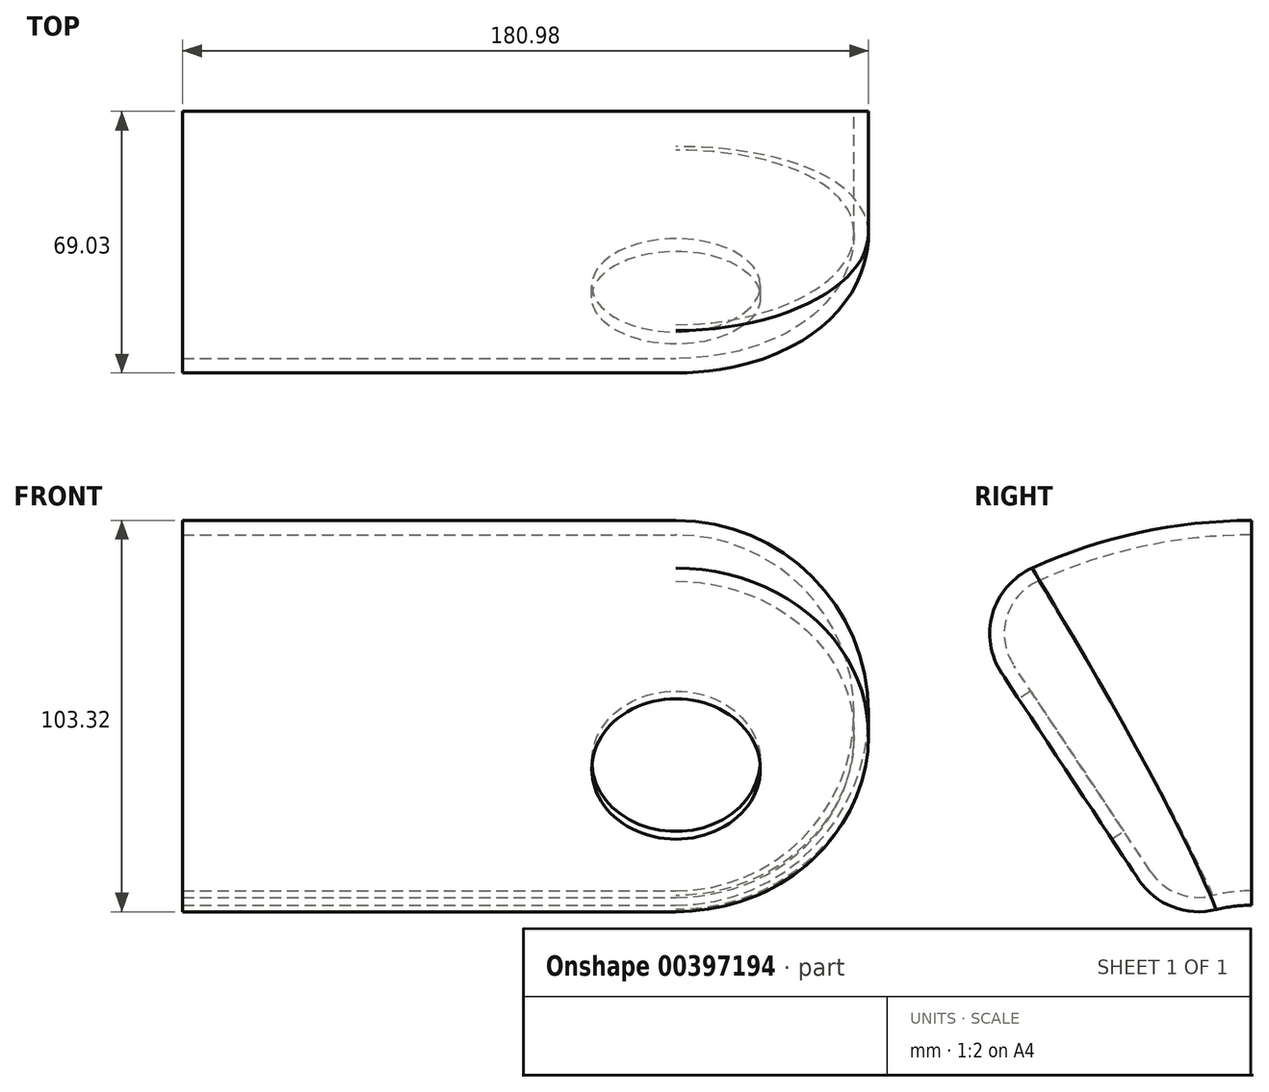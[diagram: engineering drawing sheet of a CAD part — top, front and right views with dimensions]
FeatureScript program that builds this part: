
annotation { "Feature Type Name" : "Feature", "Feature Type Description" : "" }
export const myFeature = defineFeature(function(context is Context, id is Id, definition is map)
    precondition{}
    {
        {
            var Q0;
            Q0=qCreatedBy(makeId("Front.planeOp"),FACE);
            var sketch = newSketch(context, id + "F0", { "sketchPlane" : qUnion([Q0])});
            skLineSegment(sketch, "E0.bottom", {"start": v(0, 0) * mm, "end": v(130.18, 0) * mm});
            skLineSegment(sketch, "E0.top", {"start": v(0, 101.6) * mm, "end": v(130.18, 101.6) * mm});
            skLineSegment(sketch, "E0.left", {"start": v(0, 0) * mm, "end": v(0, 101.6) * mm});
            skLineSegment(sketch, "E0.right", {"start": v(180.98, 0) * mm, "end": v(180.98, 101.6) * mm, "construction": true});
            skLineSegment(sketch, "E1", {"start": v(130.18, 101.6) * mm, "end": v(130.18, 0) * mm, "construction": true});
            skArc(sketch, "E2", {"start": v(130.18, 101.6) * mm, "mid": v(79.38, 50.8) * mm, "end": v(130.18, 0) * mm, "construction": true});
            skArc(sketch, "E3", {"start": v(130.18, 0) * mm, "mid": v(180.98, 50.8) * mm, "end": v(130.18, 101.6) * mm});
            skLineSegment(sketch, "E4", {"start": v(130.18, 101.6) * mm, "end": v(180.98, 101.6) * mm, "construction": true});
            skLineSegment(sketch, "E5", {"start": v(130.18, 0) * mm, "end": v(130.18, 0) * mm});
            skLineSegment(sketch, "E6", {"start": v(130.18, 0) * mm, "end": v(180.98, 0) * mm, "construction": true});
            skCircle(sketch, "E7", {"center": v(130.18, 50.8) * mm, "radius": 22.23 * mm});
            skSolve(sketch);
        }
        {
            var Q0;
            Q0=qCreatedBy(makeId("Right.planeOp"),FACE);
            var sketch = newSketch(context, id + "F1", { "sketchPlane" : qUnion([Q0])});
            skLineSegment(sketch, "E8", {"start": v(0, 0) * mm, "end": v(-25.4, 0) * mm});
            skArc(sketch, "E9", {"start": v(-25.4, 0) * mm, "mid": v(-36.4, -1.62) * mm, "end": v(-46.46, -6.35) * mm});
            skLineSegment(sketch, "E10", {"start": v(-25.4, 0) * mm, "end": v(-25.4, -38.1) * mm});
            skSolve(sketch);
        }
        {
            var Q0;
            Q0=makeQuery(id+"F0.imprint","IMPRINT",FACE,{"disambiguationData":[TD([[makeQuery(id+"F0.imprint","IMPRINT",EDGE,{"derivedFrom":sQuery(id+"F0.wireOp",EDGE,"E0.bottom")}),1.0]])]});
            var Q1;
            Q1=sQuery(id+"F1.wireOp",EDGE,"E8");
            var Q2;
            Q2=sQuery(id+"F1.wireOp",EDGE,"E9");
            sweep(context, id + "F2", {"profiles" : qUnion([Q0]), "path" : qUnion([Q1, Q2])});
        }
        {
            var Q0;
            Q0=makeQuery(id+"F2.opSweep","CAP_EDGE",EDGE,{"disambiguationData":[OSD([sQuery(id+"F0.wireOp",EDGE,"E0.top"),sQuery(id+"F1.wireOp",VERTEX,"E9.end")])],"isStart":false});
            fillet(context, id + "F3", {"entities" : qUnion([Q0]), "radius" : 19.05 * mm, "tangentPropagation" : true, "allowEdgeOverflow" : false});
        }
        {
            var Q0;
            Q0=makeQuery(id+"F2.opSweep","SWEPT_FACE",FACE,{"disambiguationData":[OSD([sQuery(id+"F0.wireOp",EDGE,"E0.left"),sQuery(id+"F1.wireOp",EDGE,"E8")])]});
            var Q1;
            Q1=makeQuery(id+"F2.opSweep","CAP_FACE",FACE,{"disambiguationData":[OSD([sQuery(id+"F0.wireOp",EDGE,"E0.bottom"),sQuery(id+"F0.wireOp",EDGE,"E0.top"),sQuery(id+"F0.wireOp",EDGE,"E0.left"),sQuery(id+"F0.wireOp",EDGE,"E3"),sQuery(id+"F0.wireOp",EDGE,"E7"),sQuery(id+"F1.wireOp",VERTEX,"E8.start")])],"isStart":true});
            var Q2;
            Q2=makeQuery(id+"F2.opSweep","SWEPT_FACE",FACE,{"disambiguationData":[OSD([sQuery(id+"F0.wireOp",EDGE,"E7"),sQuery(id+"F1.wireOp",EDGE,"E9")])]});
            var Q3;
            Q3=makeQuery(id+"F2.opSweep","SWEPT_FACE",FACE,{"disambiguationData":[OSD([sQuery(id+"F0.wireOp",EDGE,"E7"),sQuery(id+"F1.wireOp",EDGE,"E8")])]});
            shell(context, id + "F4", {"entities" : qUnion([Q0, Q1, Q2, Q3]), "thickness" : 3.8 * mm});
        }
    });
